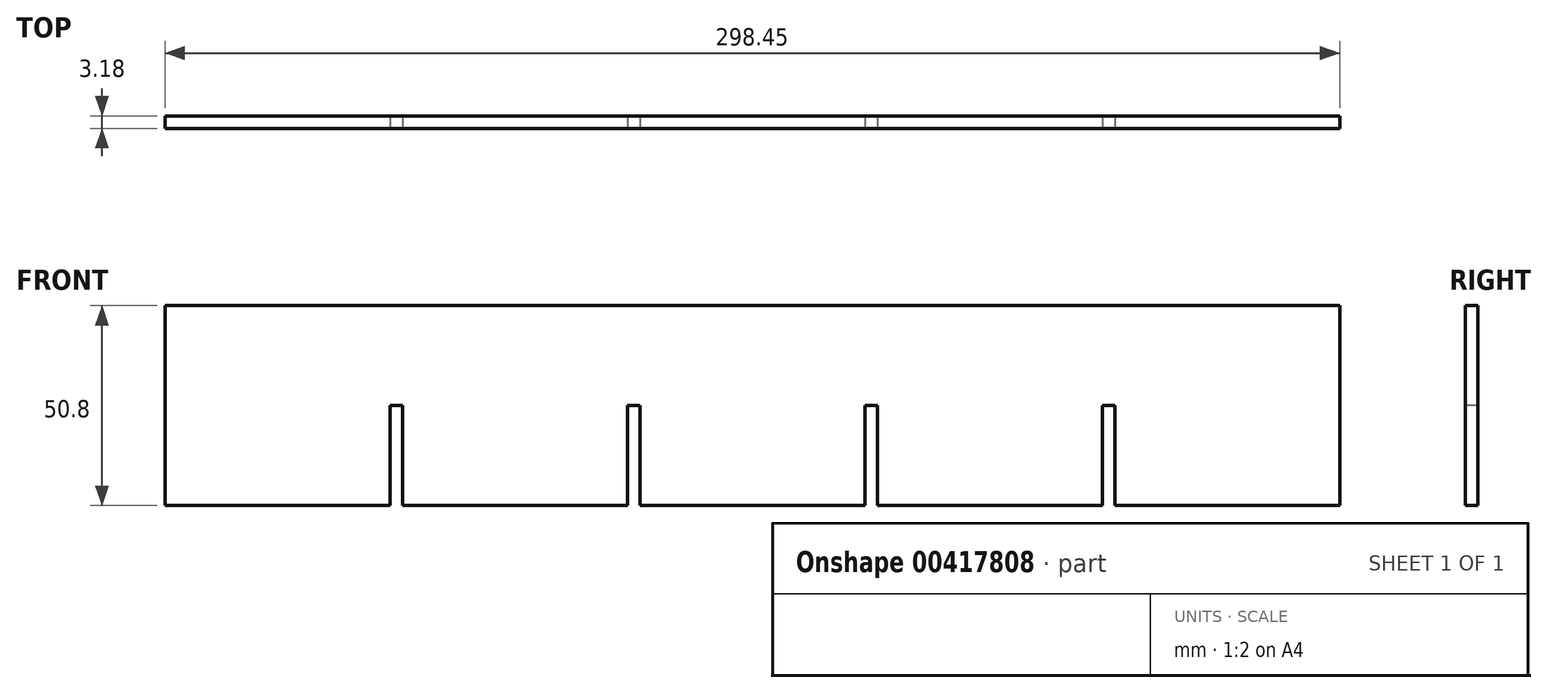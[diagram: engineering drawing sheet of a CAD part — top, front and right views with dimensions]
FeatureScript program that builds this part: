
annotation { "Feature Type Name" : "Feature", "Feature Type Description" : "" }
export const myFeature = defineFeature(function(context is Context, id is Id, definition is map)
    precondition{}
    {
        {
            var Q0;
            Q0=qCreatedBy(makeId("Front.planeOp"),FACE);
            var sketch = newSketch(context, id + "F0", { "sketchPlane" : qUnion([Q0])});
            skLineSegment(sketch, "E0.bottom", {"start": v(-151.26, 21.96) * mm, "end": v(147.2, 21.96) * mm});
            skLineSegment(sketch, "E0.top", {"start": v(-151.26, -28.84) * mm, "end": v(147.2, -28.84) * mm});
            skLineSegment(sketch, "E0.left", {"start": v(-151.26, 21.96) * mm, "end": v(-151.26, -28.84) * mm});
            skLineSegment(sketch, "E0.right", {"start": v(147.2, 21.96) * mm, "end": v(147.2, -28.84) * mm});
            skSolve(sketch);
        }
        {
            var Q0;
            Q0=makeQuery(id+"F0.imprint","IMPRINT",FACE,{"disambiguationData":[TD([[makeQuery(id+"F0.imprint","IMPRINT",EDGE,{"derivedFrom":sQuery(id+"F0.wireOp",EDGE,"E0.bottom")}),-1.0]])]});
            extrude(context, id + "F1", {"entities" : qUnion([Q0]), "depth" : 3.17 * mm});
        }
        {
            var Q0;
            Q0=makeQuery(id+"F1.opExtrude","CAP_FACE",FACE,{"disambiguationData":[OSD([sQuery(id+"F0.wireOp",EDGE,"E0.bottom"),sQuery(id+"F0.wireOp",EDGE,"E0.top"),sQuery(id+"F0.wireOp",EDGE,"E0.left"),sQuery(id+"F0.wireOp",EDGE,"E0.right")])],"isStart":false});
            var sketch = newSketch(context, id + "F2", { "sketchPlane" : qUnion([Q0])});
            skLineSegment(sketch, "E1.bottom", {"start": v(-94.1, -28.84) * mm, "end": v(-90.93, -28.84) * mm});
            skLineSegment(sketch, "E1.top", {"start": v(-94.1, -3.44) * mm, "end": v(-90.93, -3.44) * mm});
            skLineSegment(sketch, "E1.left", {"start": v(-94.1, -28.84) * mm, "end": v(-94.1, -3.44) * mm});
            skLineSegment(sketch, "E1.right", {"start": v(-90.93, -28.84) * mm, "end": v(-90.93, -3.44) * mm});
            skLineSegment(sketch, "E2.bottom", {"start": v(-33.78, -28.84) * mm, "end": v(-30.6, -28.84) * mm});
            skLineSegment(sketch, "E2.top", {"start": v(-33.78, -3.44) * mm, "end": v(-30.6, -3.44) * mm});
            skLineSegment(sketch, "E2.left", {"start": v(-33.78, -28.84) * mm, "end": v(-33.78, -3.44) * mm});
            skLineSegment(sketch, "E2.right", {"start": v(-30.6, -28.84) * mm, "end": v(-30.6, -3.44) * mm});
            skLineSegment(sketch, "E3.bottom", {"start": v(26.54, -28.84) * mm, "end": v(29.72, -28.84) * mm});
            skLineSegment(sketch, "E3.top", {"start": v(26.54, -3.44) * mm, "end": v(29.72, -3.44) * mm});
            skLineSegment(sketch, "E3.left", {"start": v(26.54, -28.84) * mm, "end": v(26.54, -3.44) * mm});
            skLineSegment(sketch, "E3.right", {"start": v(29.72, -28.84) * mm, "end": v(29.72, -3.44) * mm});
            skLineSegment(sketch, "E4.bottom", {"start": v(86.87, -28.84) * mm, "end": v(90.04, -28.84) * mm});
            skLineSegment(sketch, "E4.top", {"start": v(86.87, -3.44) * mm, "end": v(90.04, -3.44) * mm});
            skLineSegment(sketch, "E4.left", {"start": v(86.87, -28.84) * mm, "end": v(86.87, -3.44) * mm});
            skLineSegment(sketch, "E4.right", {"start": v(90.04, -28.84) * mm, "end": v(90.04, -3.44) * mm});
            skSolve(sketch);
        }
        {
            var Q0;
            Q0=makeQuery(id+"F2.imprint","IMPRINT",FACE,{"disambiguationData":[TD([[makeQuery(id+"F2.imprint","IMPRINT",EDGE,{"derivedFrom":sQuery(id+"F2.wireOp",EDGE,"E1.bottom")}),1.0]])]});
            var Q1;
            Q1=makeQuery(id+"F2.imprint","IMPRINT",FACE,{"disambiguationData":[TD([[makeQuery(id+"F2.imprint","IMPRINT",EDGE,{"derivedFrom":sQuery(id+"F2.wireOp",EDGE,"E2.bottom")}),1.0]])]});
            var Q2;
            Q2=makeQuery(id+"F2.imprint","IMPRINT",FACE,{"disambiguationData":[TD([[makeQuery(id+"F2.imprint","IMPRINT",EDGE,{"derivedFrom":sQuery(id+"F2.wireOp",EDGE,"E3.bottom")}),1.0]])]});
            var Q3;
            Q3=makeQuery(id+"F2.imprint","IMPRINT",FACE,{"disambiguationData":[TD([[makeQuery(id+"F2.imprint","IMPRINT",EDGE,{"derivedFrom":sQuery(id+"F2.wireOp",EDGE,"E4.bottom")}),1.0]])]});
            extrude(context, id + "F3", {"entities" : qUnion([Q0, Q1, Q2, Q3]), "operationType" : NewBodyOperationType.REMOVE, "oppositeDirection" : true, "depth" : 25.4 * mm});
        }
    });
